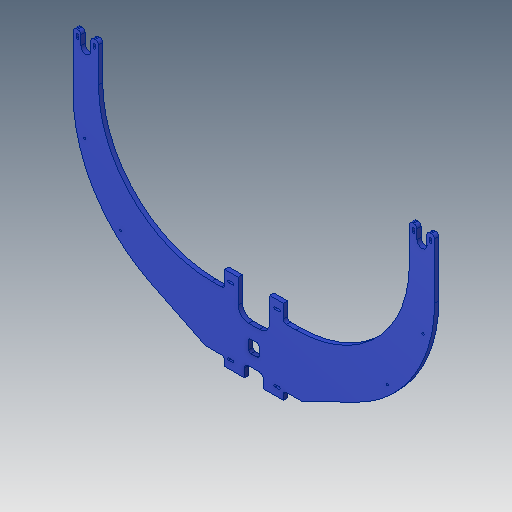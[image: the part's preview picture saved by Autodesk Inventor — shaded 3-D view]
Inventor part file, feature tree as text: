
AUTODESK INVENTOR PART (.ipt)
format: ipt  version: 2023.5 (Build 275446000, 446)  size: 169,984 bytes
history: native  units: in
note: dims shown in document units (in); Inventor stores cm internally (conversion verified against a paired STEP export)
features: fillet x1
ambient origin geometry x8: Origin, YZ Plane, XZ Plane, XY Plane, X Axis, Y Axis, Z Axis, Center Point
bodies: Solid1 (feature_tree)
feature tree (1):
  fillet  "Fillet5"  [1 undecoded]
note: 1 required parameter value undecoded (feature->parameter linkage not recoverable at this tier; creation-order binding heuristic only, values carry confidence <= 0.55)
